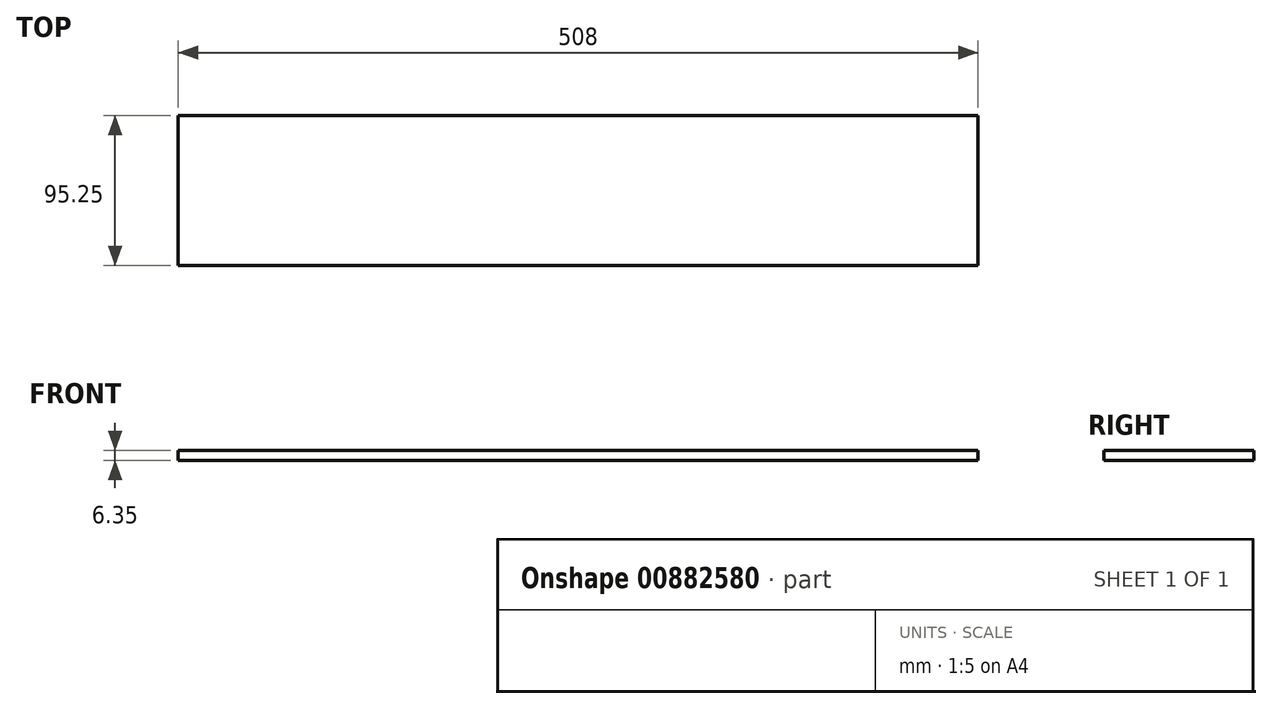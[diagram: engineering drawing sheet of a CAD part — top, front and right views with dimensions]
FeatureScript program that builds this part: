
annotation { "Feature Type Name" : "Feature", "Feature Type Description" : "" }
export const myFeature = defineFeature(function(context is Context, id is Id, definition is map)
    precondition{}
    {
        {
            var Q0;
            Q0=qCreatedBy(makeId("Right.planeOp"),FACE);
            var sketch = newSketch(context, id + "F0", { "sketchPlane" : qUnion([Q0])});
            skLineSegment(sketch, "E0.bottom", {"start": v(0, 0) * mm, "end": v(95.25, 0) * mm});
            skLineSegment(sketch, "E0.top", {"start": v(0, -6.35) * mm, "end": v(95.25, -6.35) * mm});
            skLineSegment(sketch, "E0.left", {"start": v(0, 0) * mm, "end": v(0, -6.35) * mm});
            skLineSegment(sketch, "E0.right", {"start": v(95.25, 0) * mm, "end": v(95.25, -6.35) * mm});
            skSolve(sketch);
        }
        {
            var Q0;
            Q0 = qSketchRegion(id + "F0", true);
            extrude(context, id + "F1", {"entities" : qUnion([Q0]), "depth" : 508 * mm, "offsetDistance" : 25.4 * mm});
        }
    });
